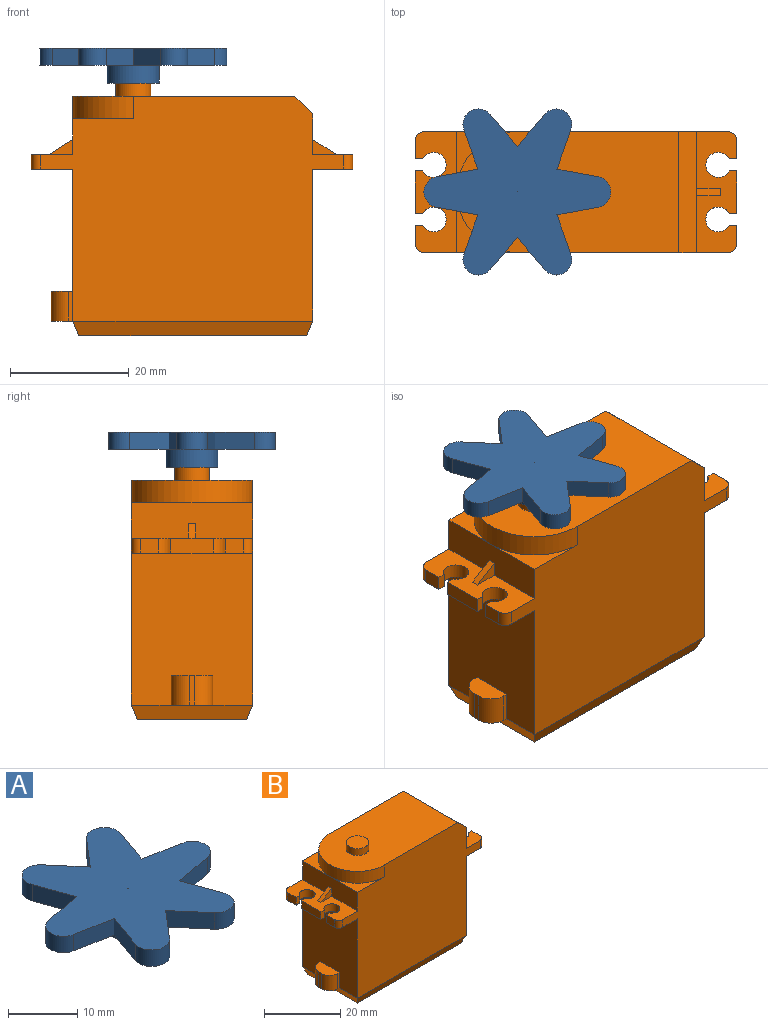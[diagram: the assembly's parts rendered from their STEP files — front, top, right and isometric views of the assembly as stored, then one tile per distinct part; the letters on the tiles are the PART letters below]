
ASSEMBLY  parts=2 mates=1
PART A: 27 faces, bbox 31.5x28x5.9 mm
  f0: plane 5.87x5.87mm, normal (0,0,-1), area 27.1mm2, adj f1,f2,f21,f25
  f1: plane 2.9x0mm, normal (-0.87,-0.5,0), area 0mm2, adj f0,f2,f21,f22
  f2: plane 2.9x0mm, normal (-0.87,0.5,0), area 0mm2, adj f0,f1,f21,f22
  f3: plane 6.67x2.9mm, normal (-0.94,0.33,0), area 20.5mm2, adj f4,f20,f22,f23
  f4: cylinder r=2.6mm len=4.58mm, axis (0,0,-1), area 20.9mm2, adj f3,f5,f22,f23
  f5: plane 5.38x4.6mm, normal (0.76,-0.65,0), area 20.5mm2, adj f4,f6,f22,f23
  f6: plane 5.38x4.6mm, normal (-0.76,-0.65,0), area 20.5mm2, adj f5,f7,f22,f23
  f7: cylinder r=2.6mm len=4.58mm, axis (0,0,-1), area 20.9mm2, adj f6,f8,f22,f23
  f8: plane 6.67x2.9mm, normal (0.94,0.33,0), area 20.5mm2, adj f7,f9,f22,f23
  f9: plane 6.96x2.9mm, normal (0.18,-0.98,0), area 20.5mm2, adj f8,f10,f22,f23
  f10: cylinder r=2.6mm len=5.11mm, axis (0,0,-1), area 20.9mm2, adj f9,f11,f22,f23
  f11: plane 6.96x2.9mm, normal (0.18,0.98,0), area 20.5mm2, adj f10,f12,f22,f23
  f12: plane 6.67x2.9mm, normal (0.94,-0.33,0), area 20.5mm2, adj f11,f13,f22,f23
  f13: cylinder r=2.6mm len=4.58mm, axis (0,0,-1), area 20.9mm2, adj f12,f14,f22,f23
  f14: plane 5.38x4.6mm, normal (-0.76,0.65,0), area 20.5mm2, adj f13,f15,f22,f23
  f15: plane 5.38x4.6mm, normal (0.76,0.65,0), area 20.5mm2, adj f14,f16,f22,f23
  f16: cylinder r=2.6mm len=4.58mm, axis (0,0,-1), area 20.9mm2, adj f15,f17,f22,f23
  f17: plane 6.67x2.9mm, normal (-0.94,-0.33,0), area 20.5mm2, adj f16,f18,f22,f23
  f18: plane 6.96x2.9mm, normal (-0.18,0.98,0), area 20.5mm2, adj f17,f19,f22,f23
  f19: cylinder r=2.6mm len=5.11mm, axis (0,0,-1), area 20.9mm2, adj f18,f20,f22,f23
  f20: plane 6.96x2.9mm, normal (-0.18,-0.98,0), area 20.5mm2, adj f3,f19,f22,f23
  f21: plane 2.9x0mm, normal (1,0,0), area 0mm2, adj f0,f1,f2,f22
  f22: plane 31.5x27.98mm, normal (0,0,1), area 470.4mm2, adj f1,f2,f3,f4,f5,f6,f7,f8
  f23: plane 31.5x27.98mm, normal (0,0,-1), area 410.3mm2, adj f3,f4,f5,f6,f7,f8,f9,f10
  f24: cylinder r=4.38mm len=8.75mm, axis (0,0,-1), area 82.5mm2, adj f23,f26
  f25: cylinder r=2.94mm len=5.87mm, axis (0,0,-1), area 55.3mm2, adj f0,f26
  f26: plane 8.75x8.75mm, normal (0,0,-1), area 33.1mm2, adj f24,f25
PART B: 57 faces, bbox 54.2x20.4x42.6 mm
  f0: plane 25.6x20.4mm, normal (-1,0,0), area 487.2mm2, adj f3,f4,f7,f46,f48,f49,f51
  f1: plane 10.2x10.2mm, normal (0,0,1), area 22.3mm2, adj f4,f28,f31
  f2: plane 20.4x7mm, normal (0,0,1), area 105mm2, adj f3,f4,f8,f9,f10,f11,f12,f13
  f3: plane 51.15x37.9mm, normal (0,1,0), area 1514.8mm2, adj f0,f2,f5,f7,f26,f27,f28,f29
  f4: plane 51.15x37.9mm, normal (0,-1,0), area 1514.8mm2, adj f0,f1,f2,f5,f7,f26,f27,f28
  f5: plane 25.6x20.4mm, normal (1,0,0), area 522.2mm2, adj f3,f4,f27,f54
  f6: plane 38.4x18.4mm, normal (0,0,-1), area 706.6mm2, adj f51,f52,f53,f54
  f7: plane 20.4x7mm, normal (0,0,-1), area 109.8mm2, adj f0,f3,f4,f8,f9,f10,f11,f12
  f8: cylinder r=2.1mm len=4.2mm, axis (0,0,-1), area 27.8mm2, adj f2,f7,f9,f25
  f9: plane 2.5x1.25mm, normal (0,1,0), area 3.1mm2, adj f2,f7,f8,f10
  f10: plane 7.2x2.5mm, normal (-1,0,0), area 18mm2, adj f2,f7,f9,f11
  f11: plane 2.5x1.25mm, normal (0,-1,0), area 3.1mm2, adj f2,f7,f10,f12
  f12: cylinder r=2.1mm len=4.2mm, axis (0,0,-1), area 27.8mm2, adj f2,f7,f11,f13
  f13: plane 2.5x1.25mm, normal (0,1,0), area 3.1mm2, adj f2,f7,f12,f14
  f14: plane 3.1x2.5mm, normal (-1,0,0), area 7.7mm2, adj f2,f7,f13,f41
  f15: plane 3.1x2.5mm, normal (1,0,0), area 7.7mm2, adj f16,f26,f27,f44
  f16: plane 2.5x1.25mm, normal (0,1,0), area 3.1mm2, adj f15,f17,f26,f27
  f17: cylinder r=2.1mm len=4.2mm, axis (0,0,-1), area 27.8mm2, adj f16,f18,f26,f27
  f18: plane 2.5x1.25mm, normal (0,-1,0), area 3.1mm2, adj f17,f19,f26,f27
  f19: plane 7.2x2.5mm, normal (1,0,0), area 18mm2, adj f18,f20,f26,f27
  f20: plane 2.5x1.25mm, normal (0,1,0), area 3.1mm2, adj f19,f21,f26,f27
  f21: cylinder r=2.1mm len=4.2mm, axis (0,0,-1), area 27.8mm2, adj f20,f22,f26,f27
  f22: plane 2.5x1.25mm, normal (0,-1,0), area 3.1mm2, adj f21,f23,f26,f27
  f23: plane 3.1x2.5mm, normal (1,0,0), area 7.7mm2, adj f22,f26,f27,f43
  f24: plane 3.1x2.5mm, normal (-1,0,0), area 7.7mm2, adj f2,f7,f25,f42
  f25: plane 2.5x1.25mm, normal (0,-1,0), area 3.1mm2, adj f2,f7,f8,f24
  f26: plane 20.4x6.75mm, normal (0,0,1), area 99.9mm2, adj f3,f4,f15,f16,f17,f18,f19,f20
  f27: plane 20.4x6.75mm, normal (0,0,-1), area 104.7mm2, adj f3,f4,f5,f15,f16,f17,f18,f19
  f28: plane 20.4x6mm, normal (-1,0,0), area 119.4mm2, adj f1,f2,f3,f4,f30,f38,f39,f40
  f29: plane 20.4x6.8mm, normal (1,0,0), area 135.7mm2, adj f3,f4,f26,f35,f36,f37,f45
  f30: plane 10.2x10.2mm, normal (0,0,1), area 22.3mm2, adj f3,f28,f31
  f31: cylinder r=10.2mm len=20.4mm, axis (0,0,-1), area 121.8mm2, adj f1,f3,f4,f30,f32
  f32: plane 37.4x20.4mm, normal (0,0,1), area 691mm2, adj f3,f4,f31,f33,f45
  f33: cylinder r=2.95mm len=5.9mm, axis (0,0,-1), area 40.8mm2, adj f32,f34
  f34: plane 5.9x5.9mm, normal (0,0,1), area 27.3mm2, adj f33
  f35: plane 4x2.49mm, normal (0.53,0,0.85), area 5.7mm2, adj f26,f29,f36,f37
  f36: plane 4x2.49mm, normal (0,-1,0), area 5mm2, adj f26,f29,f35
  f37: plane 4x2.49mm, normal (0,1,0), area 5mm2, adj f26,f29,f35
  f38: plane 4x2.5mm, normal (-0.53,0,0.85), area 5.7mm2, adj f2,f28,f39,f40
  f39: plane 4x2.5mm, normal (0,-1,0), area 5mm2, adj f2,f28,f38
  f40: plane 4x2.5mm, normal (0,1,0), area 5mm2, adj f2,f28,f38
  f41: cylinder r=1.5mm len=2.5mm, axis (0,0,1), area 5.9mm2, adj f2,f4,f7,f14
  f42: cylinder r=1.5mm len=2.5mm, axis (0,0,-1), area 5.9mm2, adj f2,f3,f7,f24
  f43: cylinder r=1.5mm len=2.5mm, axis (0,0,1), area 5.9mm2, adj f3,f23,f26,f27
  f44: cylinder r=1.5mm len=2.5mm, axis (0,0,-1), area 5.9mm2, adj f4,f15,f26,f27
  f45: plane 20.4x3mm, normal (0.71,0,0.71), area 86.5mm2, adj f3,f4,f29,f32
  f46: plane 5x0.68mm, normal (0,-1,0), area 3.4mm2, adj f0,f47,f49,f56
  f47: plane 7x3.68mm, normal (0,0,-1), area 21.9mm2, adj f46,f48,f50,f51,f55,f56
  f48: plane 5x0.68mm, normal (0,1,0), area 3.4mm2, adj f0,f47,f49,f55
  f49: plane 7x3.68mm, normal (0,0,1), area 21.9mm2, adj f0,f46,f48,f50,f55,f56
  f50: plane 5x1mm, normal (-1,0,0), area 5mm2, adj f47,f49,f55,f56
  f51: plane 20.4x2.5mm, normal (-0.93,0,-0.37), area 52.2mm2, adj f0,f6,f47,f52,f53
  f52: plane 40.4x2.5mm, normal (0,0.93,-0.37), area 106.1mm2, adj f3,f6,f51,f54
  f53: plane 40.4x2.5mm, normal (0,-0.93,-0.37), area 106.1mm2, adj f4,f6,f51,f54
  f54: plane 20.4x2.5mm, normal (0.93,0,-0.37), area 52.2mm2, adj f5,f6,f52,f53
  f55: cylinder r=3mm len=5mm, axis (0,0,-1), area 23.6mm2, adj f47,f48,f49,f50
  f56: cylinder r=3mm len=5mm, axis (0,0,1), area 23.6mm2, adj f46,f47,f49,f50
PLACE A t=(18.33,-2.73,-13.49)mm
PLACE B t=(18.33,-2.73,-13.49)mm
MATE revolute B.f31 <-> A.f24  axis (0,0,-1) through (8.46,-2.73,1.01)mm
